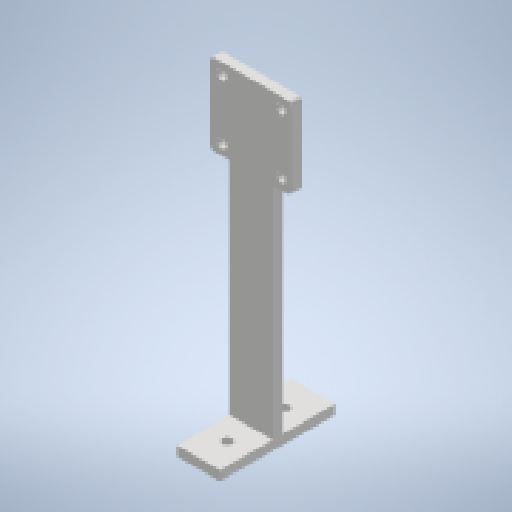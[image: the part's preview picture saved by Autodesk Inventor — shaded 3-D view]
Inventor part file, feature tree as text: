
AUTODESK INVENTOR PART (.ipt)
format: ipt  version: 2023 (Build 270158000, 158)  size: 196,608 bytes
history: native  units: mm
features: reference x9, other x6, sheet_metal_op x5, sketch x3
ambient origin geometry x8: Origin, YZ Plane, XZ Plane, XY Plane, X Axis, Y Axis, Z Axis, Center Point
bodies: Solid1 (feature_tree)
feature tree (23):
  sheet_metal_op  "Face1"
  sheet_metal_op  "Face2"
  sheet_metal_op  "Face3"
  sketch  "Sketch1"  dims[d0=2.0mm]
  reference  "Reference1"
  reference  "Reference2"
  reference  "Reference3"
  reference  "Reference4"
  reference  "Reference5"
  reference  "Reference6"
  reference  "Reference7"
  reference  "Reference8"
  other  "Plate1"
  sketch  "Sketch2"  dims[d1=5.0mm]
  reference  "Reference9"
  other  "Plate2"
  sheet_metal_op  "Bend1"
  sketch  "Sketch3"  dims[d2=22.5mm d3=115.0mm d4=110.809989mm d5=5.0mm d6=5.0mm d7=2.5mm d8=10.0mm d9=5.0mm d10=22.5mm d11=30.0mm d12=30.0mm d13=5.1mm d15=5.0mm d16=5.0mm d17=2.5mm d18=10.0mm d19=5.0mm]
  other  "Plate3"
  sheet_metal_op  "Bend2"
  other  "ensamble_general.iam"
  other  "stepper_MIR:1"
  other  "cremallera1_MIR:1"
